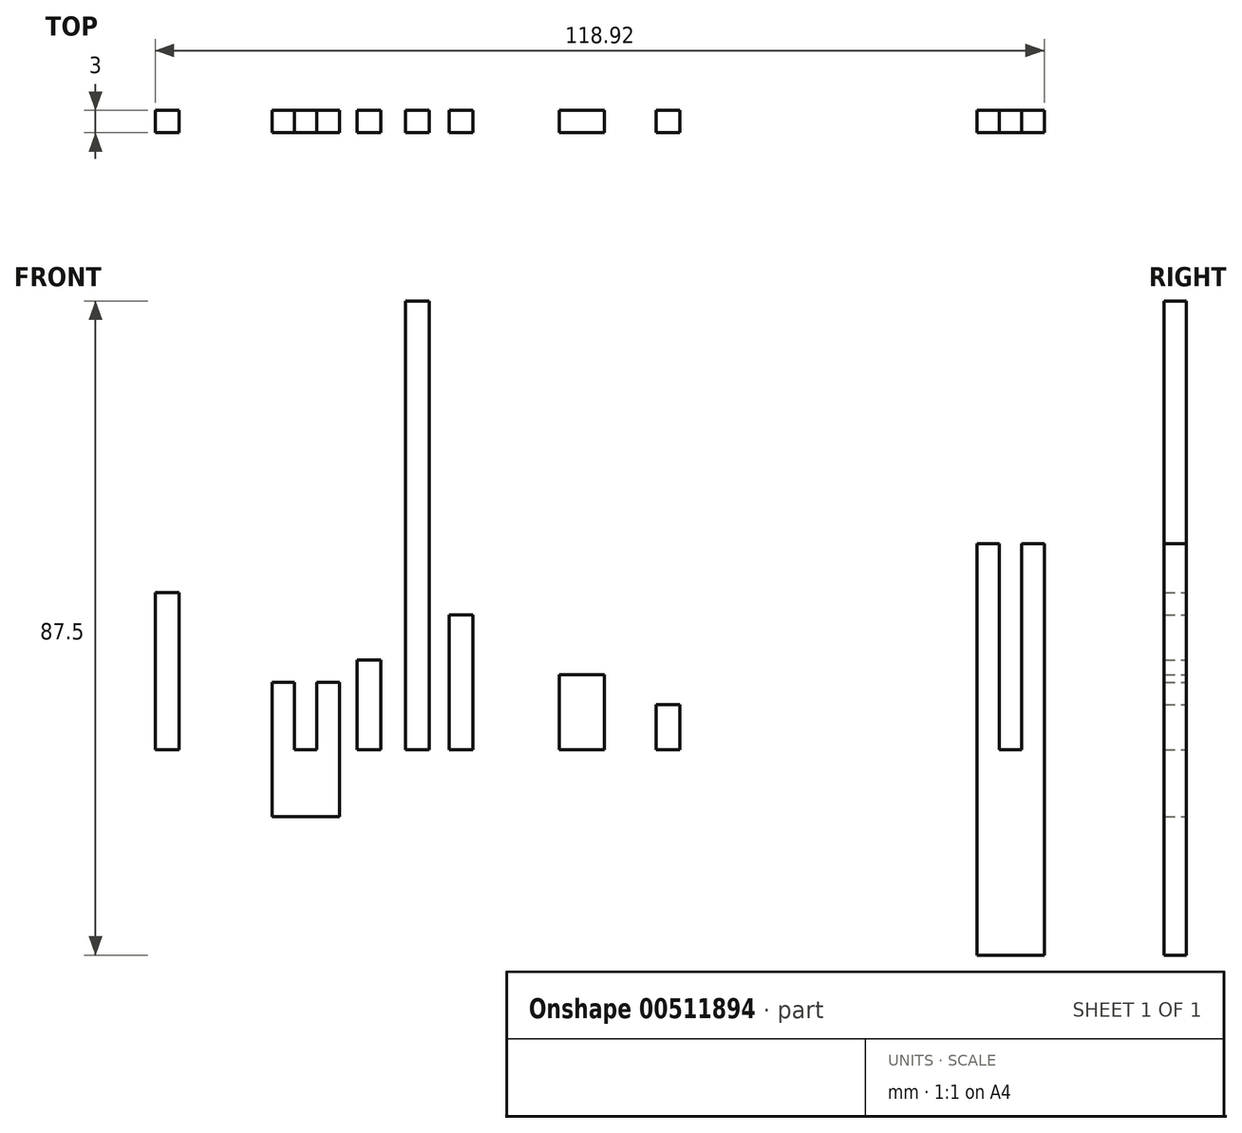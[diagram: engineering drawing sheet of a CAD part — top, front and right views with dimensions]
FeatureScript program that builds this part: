
annotation { "Feature Type Name" : "Feature", "Feature Type Description" : "" }
export const myFeature = defineFeature(function(context is Context, id is Id, definition is map)
    precondition{}
    {
        {
            var Q0;
            Q0=qCreatedBy(makeId("Front.planeOp"),FACE);
            var sketch = newSketch(context, id + "F0", { "sketchPlane" : qUnion([Q0])});
            skLineSegment(sketch, "E0.bottom", {"start": v(0, 0) * mm, "end": v(3.17, 0) * mm});
            skLineSegment(sketch, "E0.top", {"start": v(0, 60) * mm, "end": v(3.17, 60) * mm});
            skLineSegment(sketch, "E0.left", {"start": v(0, 0) * mm, "end": v(0, 60) * mm});
            skLineSegment(sketch, "E0.right", {"start": v(3.17, 0) * mm, "end": v(3.17, 60) * mm});
            skSolve(sketch);
        }
        {
            var Q0;
            Q0=makeQuery(id+"F0.imprint","IMPRINT",FACE,{"disambiguationData":[TD([[makeQuery(id+"F0.imprint","IMPRINT",EDGE,{"derivedFrom":sQuery(id+"F0.wireOp",EDGE,"E0.bottom")}),1.0]])]});
            extrude(context, id + "F1", {"entities" : qUnion([Q0]), "depth" : 3 * mm, "offsetDistance" : 25 * mm});
        }
        {
            var Q0;
            Q0=qCreatedBy(makeId("Front.planeOp"),FACE);
            var sketch = newSketch(context, id + "F2", { "sketchPlane" : qUnion([Q0])});
            skLineSegment(sketch, "E1.bottom", {"start": v(5.83, 0) * mm, "end": v(9, 0) * mm});
            skLineSegment(sketch, "E1.top", {"start": v(5.83, 18) * mm, "end": v(9, 18) * mm});
            skLineSegment(sketch, "E1.left", {"start": v(5.83, 0) * mm, "end": v(5.83, 18) * mm});
            skLineSegment(sketch, "E1.right", {"start": v(9, 0) * mm, "end": v(9, 18) * mm});
            skSolve(sketch);
        }
        {
            var Q0;
            Q0=makeQuery(id+"F2.imprint","IMPRINT",FACE,{"disambiguationData":[TD([[makeQuery(id+"F2.imprint","IMPRINT",EDGE,{"derivedFrom":sQuery(id+"F2.wireOp",EDGE,"E1.bottom")}),1.0]])]});
            extrude(context, id + "F3", {"entities" : qUnion([Q0]), "depth" : 3 * mm, "offsetDistance" : 25 * mm});
        }
        {
            var Q0;
            Q0=qCreatedBy(makeId("Front.planeOp"),FACE);
            var sketch = newSketch(context, id + "F4", { "sketchPlane" : qUnion([Q0])});
            skLineSegment(sketch, "E2.bottom", {"start": v(20.56, 0) * mm, "end": v(26.56, 0) * mm});
            skLineSegment(sketch, "E2.top", {"start": v(20.56, 10) * mm, "end": v(26.56, 10) * mm});
            skLineSegment(sketch, "E2.left", {"start": v(20.56, 0) * mm, "end": v(20.56, 10) * mm});
            skLineSegment(sketch, "E2.right", {"start": v(26.56, 0) * mm, "end": v(26.56, 10) * mm});
            skSolve(sketch);
        }
        {
            var Q0;
            Q0=makeQuery(id+"F4.imprint","IMPRINT",FACE,{"disambiguationData":[TD([[makeQuery(id+"F4.imprint","IMPRINT",EDGE,{"derivedFrom":sQuery(id+"F4.wireOp",EDGE,"E2.bottom")}),1.0]])]});
            extrude(context, id + "F5", {"entities" : qUnion([Q0]), "depth" : 3 * mm, "offsetDistance" : 25 * mm});
        }
        {
            var Q0;
            Q0=qCreatedBy(makeId("Front.planeOp"),FACE);
            var sketch = newSketch(context, id + "F6", { "sketchPlane" : qUnion([Q0])});
            skLineSegment(sketch, "E3.bottom", {"start": v(-6.54, 0) * mm, "end": v(-3.36, 0) * mm});
            skLineSegment(sketch, "E3.top", {"start": v(-6.54, 12) * mm, "end": v(-3.36, 12) * mm});
            skLineSegment(sketch, "E3.left", {"start": v(-6.54, 0) * mm, "end": v(-6.54, 12) * mm});
            skLineSegment(sketch, "E3.right", {"start": v(-3.36, 0) * mm, "end": v(-3.36, 12) * mm});
            skSolve(sketch);
        }
        {
            var Q0;
            Q0=makeQuery(id+"F6.imprint","IMPRINT",FACE,{"disambiguationData":[TD([[makeQuery(id+"F6.imprint","IMPRINT",EDGE,{"derivedFrom":sQuery(id+"F6.wireOp",EDGE,"E3.bottom")}),1.0]])]});
            extrude(context, id + "F7", {"entities" : qUnion([Q0]), "depth" : 3 * mm, "offsetDistance" : 25 * mm});
        }
        {
            var Q0;
            Q0=qCreatedBy(makeId("Front.planeOp"),FACE);
            var sketch = newSketch(context, id + "F8", { "sketchPlane" : qUnion([Q0])});
            skLineSegment(sketch, "E4.bottom", {"start": v(33.53, 0) * mm, "end": v(36.7, 0) * mm});
            skLineSegment(sketch, "E4.top", {"start": v(33.53, 6) * mm, "end": v(36.7, 6) * mm});
            skLineSegment(sketch, "E4.left", {"start": v(33.53, 0) * mm, "end": v(33.53, 6) * mm});
            skLineSegment(sketch, "E4.right", {"start": v(36.7, 0) * mm, "end": v(36.7, 6) * mm});
            skSolve(sketch);
        }
        {
            var Q0;
            Q0=makeQuery(id+"F8.imprint","IMPRINT",FACE,{"disambiguationData":[TD([[makeQuery(id+"F8.imprint","IMPRINT",EDGE,{"derivedFrom":sQuery(id+"F8.wireOp",EDGE,"E4.bottom")}),1.0]])]});
            extrude(context, id + "F9", {"entities" : qUnion([Q0]), "depth" : 3 * mm, "offsetDistance" : 25 * mm});
        }
        {
            var Q0;
            Q0=qCreatedBy(makeId("Front.planeOp"),FACE);
            var sketch = newSketch(context, id + "F10", { "sketchPlane" : qUnion([Q0])});
            skLineSegment(sketch, "E5.bottom", {"start": v(-8.87, 9) * mm, "end": v(-17.87, 9) * mm});
            skLineSegment(sketch, "E5.top", {"start": v(-8.87, -9) * mm, "end": v(-17.87, -9) * mm});
            skLineSegment(sketch, "E5.left", {"start": v(-8.87, 9) * mm, "end": v(-8.87, -9) * mm});
            skLineSegment(sketch, "E5.right", {"start": v(-17.87, 9) * mm, "end": v(-17.87, -9) * mm});
            skPoint(sketch, "E5.middle", {"position": v(-13.37, 0) * mm});
            skLineSegment(sketch, "E6.bottom", {"start": v(-14.87, 9) * mm, "end": v(-11.87, 9) * mm});
            skLineSegment(sketch, "E6.top", {"start": v(-14.87, 0) * mm, "end": v(-11.87, 0) * mm});
            skLineSegment(sketch, "E6.left", {"start": v(-14.87, 9) * mm, "end": v(-14.87, 0) * mm});
            skLineSegment(sketch, "E6.right", {"start": v(-11.87, 9) * mm, "end": v(-11.87, 0) * mm});
            skSolve(sketch);
        }
        {
            var Q0;
            Q0=makeQuery(id+"F10.imprint","IMPRINT",FACE,{"disambiguationData":[TD([[makeQuery(id+"F10.imprint","IMPRINT",EDGE,{"derivedFrom":sQuery(id+"F10.wireOp",EDGE,"E5.top")}),-1.0]])]});
            extrude(context, id + "F11", {"entities" : qUnion([Q0]), "depth" : 3 * mm, "offsetDistance" : 25 * mm});
        }
        {
            var Q0;
            Q0=qCreatedBy(makeId("Front.planeOp"),FACE);
            var sketch = newSketch(context, id + "F12", { "sketchPlane" : qUnion([Q0])});
            skLineSegment(sketch, "E7.bottom", {"start": v(-33.5, 0) * mm, "end": v(-30.32, 0) * mm});
            skLineSegment(sketch, "E7.top", {"start": v(-33.5, 21) * mm, "end": v(-30.32, 21) * mm});
            skLineSegment(sketch, "E7.left", {"start": v(-33.5, 0) * mm, "end": v(-33.5, 21) * mm});
            skLineSegment(sketch, "E7.right", {"start": v(-30.32, 0) * mm, "end": v(-30.32, 21) * mm});
            skSolve(sketch);
        }
        {
            var Q0;
            Q0=makeQuery(id+"F12.imprint","IMPRINT",FACE,{"disambiguationData":[TD([[makeQuery(id+"F12.imprint","IMPRINT",EDGE,{"derivedFrom":sQuery(id+"F12.wireOp",EDGE,"E7.bottom")}),1.0]])]});
            extrude(context, id + "F13", {"entities" : qUnion([Q0]), "depth" : 3 * mm, "offsetDistance" : 25 * mm});
        }
        {
            var Q0;
            Q0=qCreatedBy(makeId("Front.planeOp"),FACE);
            var sketch = newSketch(context, id + "F14", { "sketchPlane" : qUnion([Q0])});
            skLineSegment(sketch, "E8.bottom", {"start": v(85.43, 27.5) * mm, "end": v(76.43, 27.5) * mm});
            skLineSegment(sketch, "E8.top", {"start": v(85.43, -27.5) * mm, "end": v(76.43, -27.5) * mm});
            skLineSegment(sketch, "E8.left", {"start": v(85.43, 27.5) * mm, "end": v(85.43, -27.5) * mm});
            skLineSegment(sketch, "E8.right", {"start": v(76.43, 27.5) * mm, "end": v(76.43, -27.5) * mm});
            skPoint(sketch, "E8.middle", {"position": v(80.93, 0) * mm});
            skLineSegment(sketch, "E9.bottom", {"start": v(79.43, 27.5) * mm, "end": v(82.43, 27.5) * mm});
            skLineSegment(sketch, "E9.top", {"start": v(79.43, 0) * mm, "end": v(82.43, 0) * mm});
            skLineSegment(sketch, "E9.left", {"start": v(79.43, 27.5) * mm, "end": v(79.43, 0) * mm});
            skLineSegment(sketch, "E9.right", {"start": v(82.43, 27.5) * mm, "end": v(82.43, 0) * mm});
            skSolve(sketch);
        }
        {
            var Q0;
            Q0=makeQuery(id+"F14.imprint","IMPRINT",FACE,{"disambiguationData":[TD([[makeQuery(id+"F14.imprint","IMPRINT",EDGE,{"derivedFrom":sQuery(id+"F14.wireOp",EDGE,"E8.top")}),-1.0]])]});
            extrude(context, id + "F15", {"entities" : qUnion([Q0]), "depth" : 3 * mm, "offsetDistance" : 25 * mm});
        }
    });
